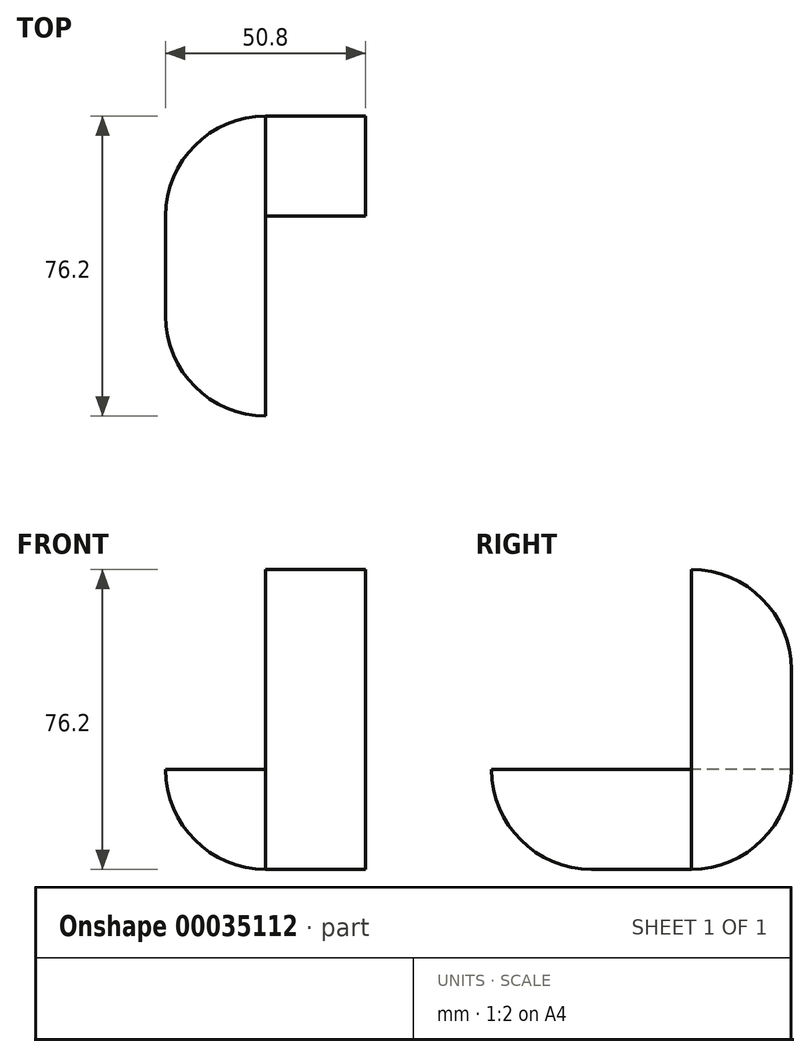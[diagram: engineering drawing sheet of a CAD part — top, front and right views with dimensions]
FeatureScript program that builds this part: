
annotation { "Feature Type Name" : "Feature", "Feature Type Description" : "" }
export const myFeature = defineFeature(function(context is Context, id is Id, definition is map)
    precondition{}
    {
        {
            var Q0;
            Q0=qCreatedBy(makeId("Top.planeOp"),FACE);
            var sketch = newSketch(context, id + "F0", { "sketchPlane" : qUnion([Q0])});
            skLineSegment(sketch, "E0", {"start": v(0, 0) * mm, "end": v(0, 76.2) * mm});
            skLineSegment(sketch, "E1", {"start": v(0, 76.2) * mm, "end": v(50.8, 76.2) * mm});
            skLineSegment(sketch, "E2", {"start": v(50.8, 76.2) * mm, "end": v(50.8, 50.8) * mm});
            skLineSegment(sketch, "E3", {"start": v(50.8, 50.8) * mm, "end": v(25.4, 50.8) * mm});
            skLineSegment(sketch, "E4", {"start": v(25.4, 50.8) * mm, "end": v(25.4, 0) * mm});
            skLineSegment(sketch, "E5", {"start": v(25.4, 0) * mm, "end": v(0, 0) * mm});
            skSolve(sketch);
        }
        {
            var Q0;
            Q0=makeQuery(id+"F0.imprint","IMPRINT",FACE,{"disambiguationData":[TD([[makeQuery(id+"F0.imprint","IMPRINT",EDGE,{"derivedFrom":sQuery(id+"F0.wireOp",EDGE,"E0")}),-1.0]])]});
            extrude(context, id + "F1", {"entities" : qUnion([Q0]), "depth" : 25.4 * mm});
        }
        {
            var Q0;
            Q0=makeQuery(id+"F1.opExtrude","CAP_FACE",FACE,{"disambiguationData":[OSD([sQuery(id+"F0.wireOp",EDGE,"E0"),sQuery(id+"F0.wireOp",EDGE,"E1"),sQuery(id+"F0.wireOp",EDGE,"E2"),sQuery(id+"F0.wireOp",EDGE,"E3"),sQuery(id+"F0.wireOp",EDGE,"E4"),sQuery(id+"F0.wireOp",EDGE,"E5")])],"isStart":false});
            var sketch = newSketch(context, id + "F2", { "sketchPlane" : qUnion([Q0])});
            skLineSegment(sketch, "E6", {"start": v(50.8, 76.2) * mm, "end": v(25.4, 76.2) * mm});
            skLineSegment(sketch, "E7", {"start": v(25.4, 76.2) * mm, "end": v(25.4, 50.8) * mm});
            skLineSegment(sketch, "E8", {"start": v(25.4, 50.8) * mm, "end": v(50.8, 50.8) * mm});
            skLineSegment(sketch, "E9", {"start": v(50.8, 50.8) * mm, "end": v(50.8, 76.2) * mm});
            skSolve(sketch);
        }
        {
            var Q0;
            Q0=makeQuery(id+"F2.imprint","IMPRINT",FACE,{"disambiguationData":[TD([[makeQuery(id+"F2.imprint","IMPRINT",EDGE,{"derivedFrom":sQuery(id+"F2.wireOp",EDGE,"E6")}),-1.0]])]});
            extrude(context, id + "F3", {"entities" : qUnion([Q0]), "operationType" : NewBodyOperationType.ADD, "depth" : 50.8 * mm});
        }
        {
            var Q0;
            Q0=makeQuery(id+"F1.opExtrude","CAP_EDGE",EDGE,{"disambiguationData":[OSD([sQuery(id+"F0.wireOp",EDGE,"E0")])],"isStart":true});
            var Q1;
            Q1=makeQuery(id+"F1.opExtrude","SWEPT_EDGE",EDGE,{"disambiguationData":[OSD([sQuery(id+"F0.wireOp",EDGE,"E0"),sQuery(id+"F0.wireOp",EDGE,"E5")])]});
            var Q2;
            Q2=makeQuery(id+"F1.opExtrude","SWEPT_EDGE",EDGE,{"disambiguationData":[OSD([sQuery(id+"F0.wireOp",EDGE,"E0"),sQuery(id+"F0.wireOp",EDGE,"E1")])]});
            var Q3;
            Q3=makeQuery(id+"F1.opExtrude","CAP_EDGE",EDGE,{"disambiguationData":[OSD([sQuery(id+"F0.wireOp",EDGE,"E1")])],"isStart":true});
            var Q4;
            Q4=makeQuery(id+"F3.opExtrude","CAP_EDGE",EDGE,{"disambiguationData":[OSD([sQuery(id+"F2.wireOp",EDGE,"E6")])],"isStart":false});
            var Q5;
            Q5=makeQuery(id+"F1.opExtrude","CAP_EDGE",EDGE,{"disambiguationData":[OSD([sQuery(id+"F0.wireOp",EDGE,"E5")])],"isStart":true});
            fillet(context, id + "F4", {"entities" : qUnion([Q0, Q1, Q2, Q3, Q4, Q5]), "radius" : 25.4 * mm, "tangentPropagation" : true, "allowEdgeOverflow" : false});
        }
    });
